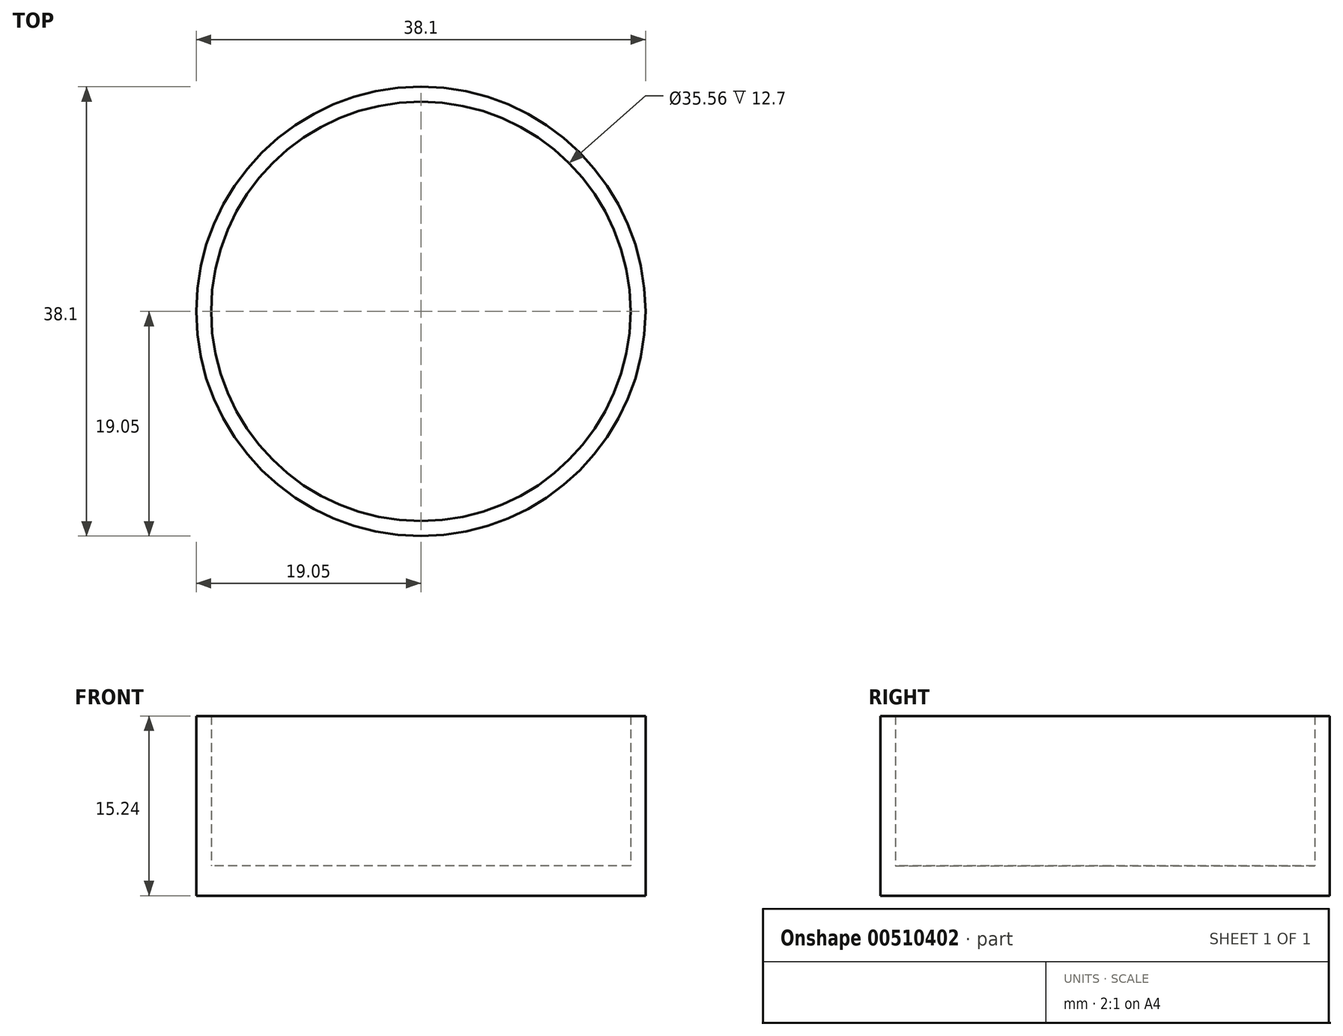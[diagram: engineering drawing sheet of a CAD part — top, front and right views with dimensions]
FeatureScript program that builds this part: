
annotation { "Feature Type Name" : "Feature", "Feature Type Description" : "" }
export const myFeature = defineFeature(function(context is Context, id is Id, definition is map)
    precondition{}
    {
        {
            var Q0;
            Q0=qCreatedBy(makeId("Top.planeOp"),FACE);
            var sketch = newSketch(context, id + "F0", { "sketchPlane" : qUnion([Q0])});
            skCircle(sketch, "E0", {"center": v(0, 0) * mm, "radius": 19.05 * mm});
            skCircle(sketch, "E1", {"center": v(0, 0) * mm, "radius": 17.78 * mm});
            skSolve(sketch);
        }
        {
            var Q0;
            Q0=qSketchRegion(id+"F0",true);
            extrude(context, id + "F1", {"entities" : qUnion([Q0]), "depth" : 12.7 * mm});
        }
        {
            var Q0;
            Q0=qCreatedBy(makeId("Top.planeOp"),FACE);
            var sketch = newSketch(context, id + "F2", { "sketchPlane" : qUnion([Q0])});
            skCircle(sketch, "E2", {"center": v(0, 0) * mm, "radius": 19.05 * mm});
            skSolve(sketch);
        }
        {
            var Q0;
            Q0=qSketchRegion(id+"F2",true);
            extrude(context, id + "F3", {"entities" : qUnion([Q0]), "operationType" : NewBodyOperationType.ADD, "oppositeDirection" : true, "depth" : 2.54 * mm});
        }
    });
